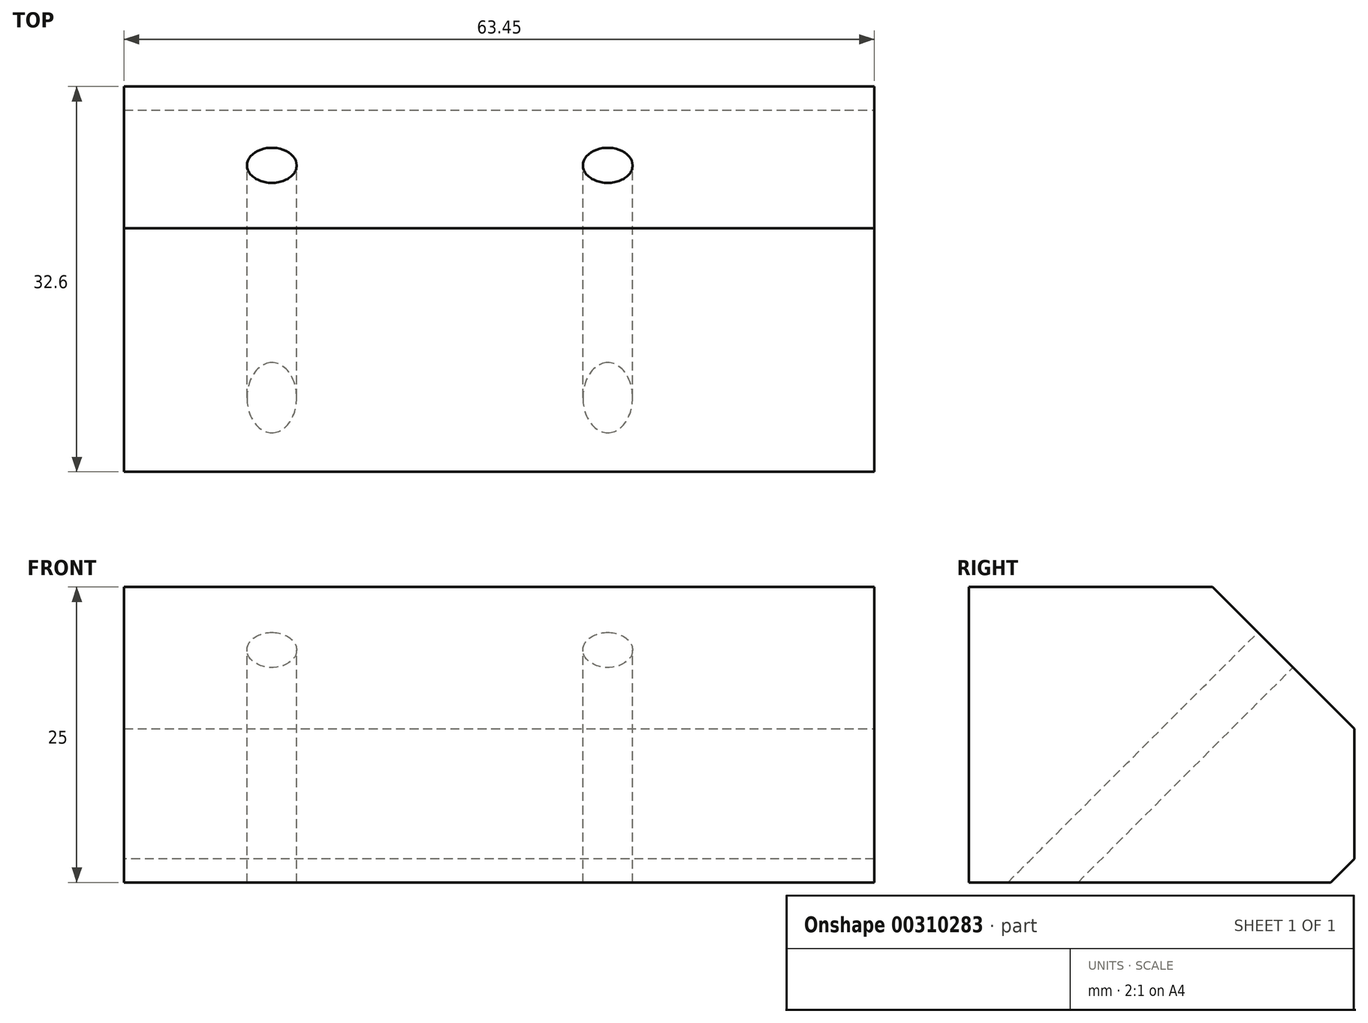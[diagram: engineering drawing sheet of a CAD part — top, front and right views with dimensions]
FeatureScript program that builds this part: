
annotation { "Feature Type Name" : "Feature", "Feature Type Description" : "" }
export const myFeature = defineFeature(function(context is Context, id is Id, definition is map)
    precondition{}
    {
        {
            var Q0;
            Q0=qCreatedBy(makeId("Top.planeOp"),FACE);
            var sketch = newSketch(context, id + "F0", { "sketchPlane" : qUnion([Q0])});
            skLineSegment(sketch, "E0.bottom", {"start": v(0, 0) * mm, "end": v(63.45, 0) * mm});
            skLineSegment(sketch, "E0.top", {"start": v(0, 32.6) * mm, "end": v(63.45, 32.6) * mm});
            skLineSegment(sketch, "E0.left", {"start": v(0, 0) * mm, "end": v(0, 32.6) * mm});
            skLineSegment(sketch, "E0.right", {"start": v(63.45, 0) * mm, "end": v(63.45, 32.6) * mm});
            skSolve(sketch);
        }
        {
            var Q0;
            Q0=makeQuery(id+"F0.imprint","IMPRINT",FACE,{"disambiguationData":[TD([[makeQuery(id+"F0.imprint","IMPRINT",EDGE,{"derivedFrom":sQuery(id+"F0.wireOp",EDGE,"E0.bottom")}),1.0]])]});
            extrude(context, id + "F1", {"entities" : qUnion([Q0]), "depth" : 25 * mm});
        }
        {
            var Q0;
            Q0=makeQuery(id+"F1.opExtrude","CAP_EDGE",EDGE,{"disambiguationData":[OSD([sQuery(id+"F0.wireOp",EDGE,"E0.top")])],"isStart":false});
            chamfer(context, id + "F2", {"entities" : qUnion([Q0]), "width" : 12 * mm, "tangentPropagation" : true});
        }
        {
            var Q0;
            Q0=makeQuery(id+"F2.opChamfer","BLEND_FACE",FACE,{"disambiguationData":[OSD([sQuery(id+"F0.wireOp",EDGE,"E0.top")])]});
            var sketch = newSketch(context, id + "F3", { "sketchPlane" : qUnion([Q0])});
            skPoint(sketch, "E1", {"position": v(-12.5, -4.43) * mm});
            skPoint(sketch, "E2", {"position": v(-40.9, -4.43) * mm});
            skSolve(sketch);
        }
        {
            var Q0;
            Q0=sQuery(id+"F3.wireOp",VERTEX,"E1");
            var Q1;
            Q1=sQuery(id+"F3.wireOp",VERTEX,"E2");
            var Q2;
            Q2=makeQuery(id+"F1.opExtrude","SWEPT_BODY",BODY,{"disambiguationData":[OSD([sQuery(id+"F0.wireOp",EDGE,"E0.bottom"),sQuery(id+"F0.wireOp",EDGE,"E0.top"),sQuery(id+"F0.wireOp",EDGE,"E0.left"),sQuery(id+"F0.wireOp",EDGE,"E0.right")])]});
            hole(context, id + "F4", {"style" : HoleStyle.SIMPLE, "endStyle" : HoleEndStyle.THROUGH, "standardTappedOrClearance" : lookupTablePath({ "standard" : "ISO", "engagement" : "75%", "pitch" : "0.8 mm", "size" : "M5", "type" : "Tapped" }), "standardBlindInLast" : lookupTablePath({ "standard" : "ISO", "engagement" : "75%", "pitch" : "0.8 mm", "size" : "M5", "type" : "Tapped" }), "holeDiameter" : 4.2 * mm, "showTappedDepth" : true, "tappedDepth" : 12 * mm, "tapClearance" : 3, "locations" : qUnion([Q0, Q1]), "scope" : qUnion([Q2]), "majorDiameter" : 5 * mm});
        }
        {
            var Q0;
            Q0=makeQuery(id+"F1.opExtrude","CAP_EDGE",EDGE,{"disambiguationData":[OSD([sQuery(id+"F0.wireOp",EDGE,"E0.top")])],"isStart":true});
            chamfer(context, id + "F5", {"entities" : qUnion([Q0]), "width" : 2 * mm, "tangentPropagation" : true});
        }
    });
